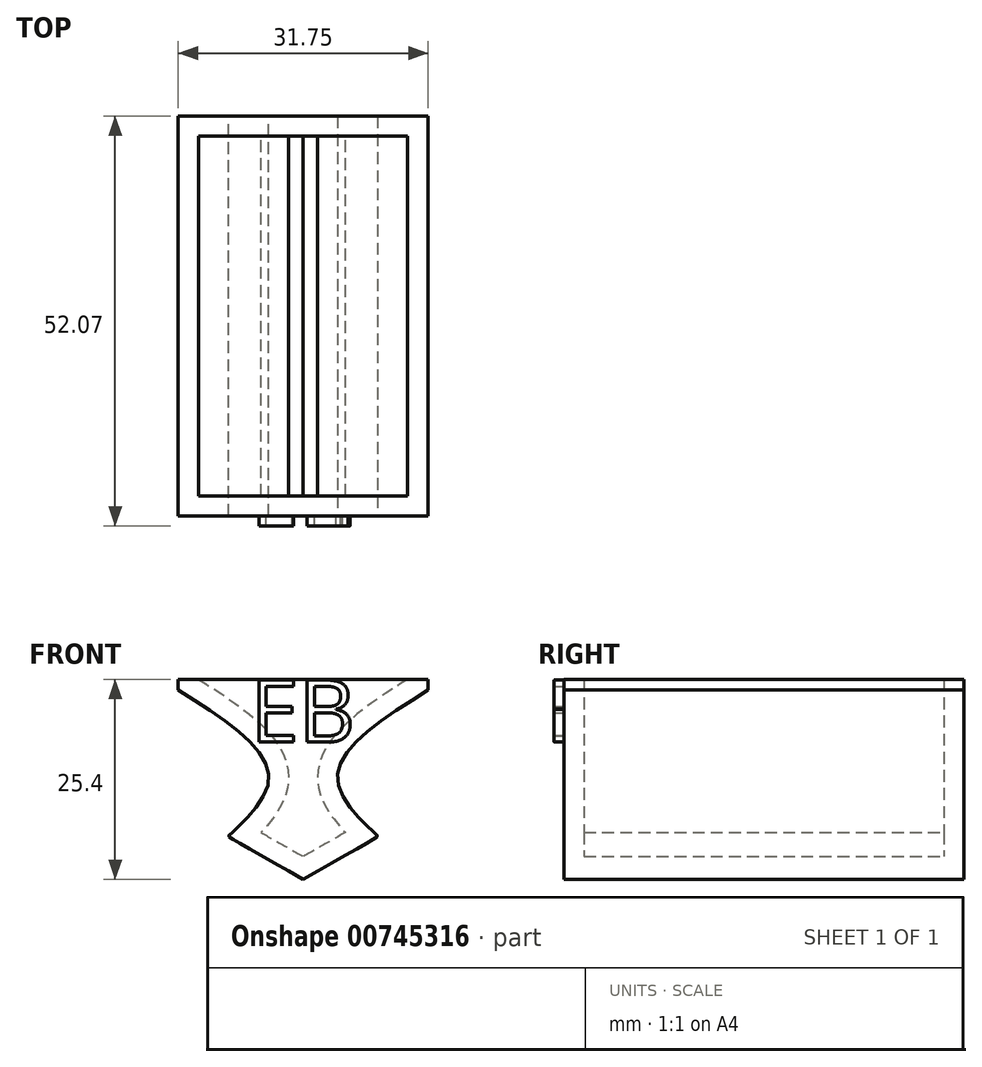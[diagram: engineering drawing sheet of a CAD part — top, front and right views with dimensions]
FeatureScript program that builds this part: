
annotation { "Feature Type Name" : "Feature", "Feature Type Description" : "" }
export const myFeature = defineFeature(function(context is Context, id is Id, definition is map)
    precondition{}
    {
        {
            var Q0;
            Q0=qCreatedBy(makeId("Front.planeOp"),FACE);
            var sketch = newSketch(context, id + "F0", { "sketchPlane" : qUnion([Q0])});
            skLineSegment(sketch, "E0.bottom", {"start": v(-25.55, 7.95) * mm, "end": v(6.2, 7.95) * mm});
            skLineSegment(sketch, "E0.top", {"start": v(-25.55, -17.45) * mm, "end": v(6.2, -17.45) * mm});
            skLineSegment(sketch, "E0.left", {"start": v(-25.55, 7.95) * mm, "end": v(-25.55, -17.45) * mm});
            skLineSegment(sketch, "E0.right", {"start": v(6.2, 7.95) * mm, "end": v(6.2, -17.45) * mm});
            skLineSegment(sketch, "E1", {"start": v(-9.68, 7.95) * mm, "end": v(-9.68, -17.45) * mm});
            skFitSpline(sketch, "E2", {"points": [v(-25.55, 6.6) * mm, v(-14.11, -5.25) * mm, v(-19.1, -11.88) * mm, v(-19.1, -11.99) * mm, v(-9.68, -17.45) * mm], "startDerivative": vector(47.78, -29.84) * mm, "endDerivative": vector(43.23, -24.36) * mm});
            skFitSpline(sketch, "E3.MirrorCS", {"points": [v(6.2, 6.6) * mm, v(-5.24, -5.25) * mm, v(-0.25, -11.88) * mm, v(-0.25, -11.99) * mm, v(-9.68, -17.45) * mm], "startDerivative": vector(-47.78, -29.84) * mm, "endDerivative": vector(-43.23, -24.36) * mm});
            skSolve(sketch);
        }
        {
            var Q0;
            {var subQ3=sQuery(id+"F0.wireOp",EDGE,"E1");Q0=makeQuery(id+"F0.imprint","IMPRINT",FACE,{"disambiguationData":[TD([[makeQuery(id+"F0.imprint","IMPRINT",EDGE,{"derivedFrom":subQ3}),1.0]])]});}
            var Q1;
            {var subQ3=sQuery(id+"F0.wireOp",EDGE,"E1");Q1=makeQuery(id+"F0.imprint","IMPRINT",FACE,{"disambiguationData":[TD([[makeQuery(id+"F0.imprint","IMPRINT",EDGE,{"derivedFrom":subQ3}),-1.0]])]});}
            extrude(context, id + "F1", {"entities" : qUnion([Q0, Q1]), "depth" : 50.8 * mm, "offsetDistance" : 25.4 * mm});
        }
        {
            var Q0;
            Q0=makeQuery(id+"F1.opExtrude","SWEPT_FACE",FACE,{"disambiguationData":[OSD([sQuery(id+"F0.wireOp",EDGE,"E0.bottom")])]});
            shell(context, id + "F2", {"entities" : qUnion([Q0]), "thickness" : 2.54 * mm});
        }
        {
            var Q0;
            Q0=makeQuery(id+"F1.opExtrude","CAP_FACE",FACE,{"disambiguationData":[OSD([sQuery(id+"F0.wireOp",EDGE,"E0.bottom"),sQuery(id+"F0.wireOp",EDGE,"E0.left"),sQuery(id+"F0.wireOp",EDGE,"E0.right"),sQuery(id+"F0.wireOp",EDGE,"E2"),sQuery(id+"F0.wireOp",EDGE,"E3.MirrorCS")])],"isStart":false});
            var sketch = newSketch(context, id + "F3", { "sketchPlane" : qUnion([Q0])});
            skText(sketch, "E4", { "text": "EB", "fontName": "OpenSans-Regular.ttf"});
            const initialGuessF3  = {"E4": [-0.01638, 0, 1, 0, 0.00795]};
            skSetInitialGuess(sketch, initialGuessF3);
            skSolve(sketch);
        }
        {
            var Q0;
            Q0 = qSketchRegion(id + "F3", true);
            extrude(context, id + "F4", {"entities" : qUnion([Q0]), "operationType" : NewBodyOperationType.ADD, "depth" : 1.27 * mm, "offsetDistance" : 25.4 * mm});
        }
    });
